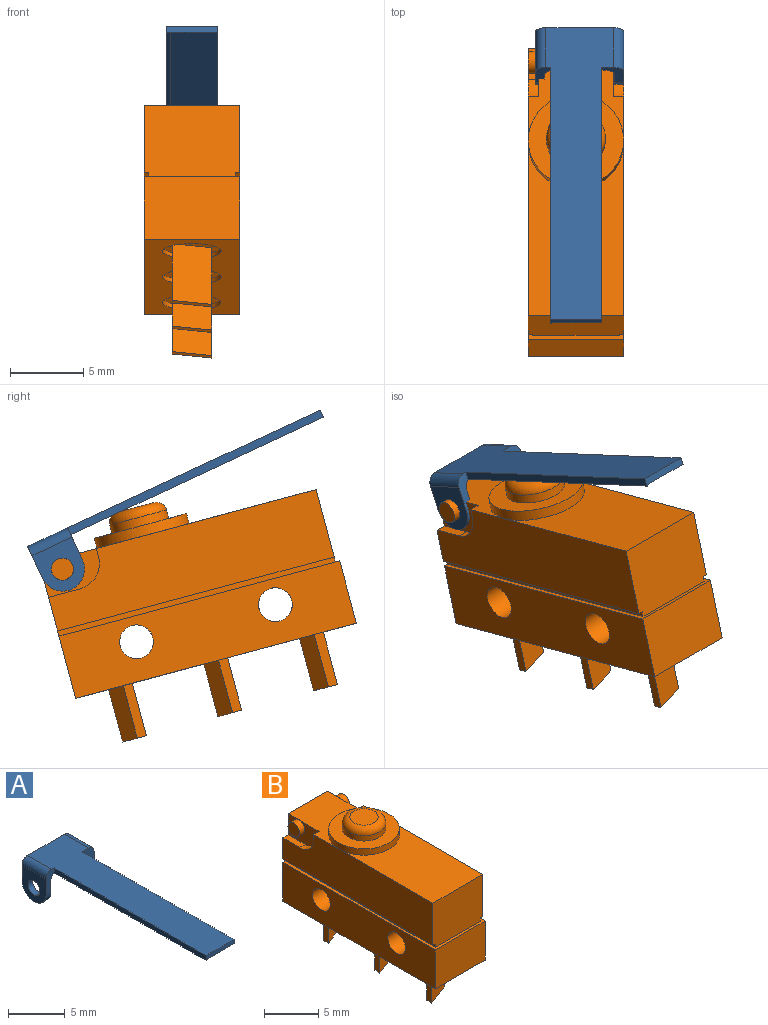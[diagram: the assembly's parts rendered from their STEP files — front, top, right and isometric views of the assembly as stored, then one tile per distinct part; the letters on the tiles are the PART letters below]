
ASSEMBLY  parts=2 mates=1
PART A: 20 faces, bbox 6x22x3.9 mm
  f0: plane 22x3.4mm, normal (0,0,-1), area 71mm2, adj f2,f3,f5,f7,f16,f17
  f1: plane 19x0.53mm, normal (-1,0,0), area 10.1mm2, adj f4,f5,f8,f16
  f2: plane 19x0.46mm, normal (1,0,0), area 8.8mm2, adj f0,f4,f5,f7
  f3: plane 6x2.4mm, normal (0,1,0), area 5.1mm2, adj f0,f4,f6,f9,f10,f12,f13,f15
  f4: plane 22x4.6mm, normal (0,0,1), area 80.3mm2, adj f1,f2,f3,f5,f7,f8,f18,f19
  f5: plane 3.5x0.53mm, normal (0,-1,0), area 1.6mm2, adj f0,f1,f2,f4,f16
  f6: plane 3.2x3mm, normal (1,0,0), area 6.9mm2, adj f3,f7,f10,f11,f18
  f7: plane 2.4x1.5mm, normal (0,-1,0), area 1.9mm2, adj f0,f2,f4,f6,f10,f12,f17,f18
  f8: plane 2.4x1mm, normal (0,-1,0), area 1.6mm2, adj f1,f4,f9,f13,f15,f16,f19
  f9: plane 3.2x3mm, normal (-1,0,0), area 6.9mm2, adj f3,f8,f13,f14,f19
  f10: cylinder r=1.5mm len=3mm, axis (1,0,0), area 2.8mm2, adj f3,f6,f7,f12
  f11: cylinder r=0.75mm len=1.5mm, axis (1,0,0), area 2.8mm2, adj f6,f12
  f12: plane 3x2.74mm, normal (-1,0,0), area 5.5mm2, adj f3,f7,f10,f11,f17
  f13: cylinder r=1.5mm len=3mm, axis (1,0,0), area 2.8mm2, adj f3,f8,f9,f15
  f14: cylinder r=0.75mm len=1.5mm, axis (1,0,0), area 2.8mm2, adj f9,f15
  f15: plane 3x2.74mm, normal (1,0,0), area 5.5mm2, adj f3,f8,f13,f14,f16
  f16: cylinder r=0.7mm len=22mm, axis (0,-1,0), area 9.2mm2, adj f0,f1,f3,f5,f8,f15
  f17: cylinder r=0.7mm len=3mm, axis (0,1,0), area 3.3mm2, adj f0,f3,f7,f12
  f18: cylinder r=0.7mm len=3mm, axis (0,-1,0), area 3.3mm2, adj f3,f4,f6,f7
  f19: cylinder r=0.7mm len=3mm, axis (0,1,0), area 3.3mm2, adj f3,f4,f8,f9
PART B: 55 faces, bbox 6.5x19.8x15.2 mm
  f0: plane 4x4mm, normal (0,0,-1), area 10.8mm2, adj f36,f50,f51,f52,f53
  f1: plane 4x4mm, normal (0,0,-1), area 10.8mm2, adj f37,f45,f46,f47,f48
  f2: plane 12.2x6.5mm, normal (0,0,1), area 62.7mm2, adj f3,f4,f6,f25
  f3: plane 19.5x4.75mm, normal (1,0,0), area 83.8mm2, adj f2,f5,f6,f8,f15,f20,f22,f24
  f4: plane 19.5x4.75mm, normal (-1,0,0), area 83.8mm2, adj f2,f5,f6,f8,f14,f18,f19,f23
  f5: plane 7.3x6.5mm, normal (0,0,1), area 25.3mm2, adj f3,f4,f8,f17,f19,f21,f22,f25
  f6: plane 6.5x5.11mm, normal (0,-1,0), area 33mm2, adj f2,f3,f4,f12,f13,f14,f15,f16
  f7: plane 19.8x4.39mm, normal (1,0,0), area 78.6mm2, adj f8,f10,f11,f12,f30,f31
  f8: plane 9.5x6.5mm, normal (0,1,0), area 58.2mm2, adj f3,f4,f5,f7,f9,f10,f12,f13
  f9: plane 19.8x4.39mm, normal (-1,0,0), area 78.6mm2, adj f8,f10,f11,f12,f30,f31
  f10: plane 19.8x6.5mm, normal (0,0,-1), area 91mm2, adj f7,f8,f9,f11,f36,f37,f38
  f11: plane 6.5x4.39mm, normal (0,-1,0), area 28.5mm2, adj f7,f9,f10,f12
  f12: plane 19.8x6.5mm, normal (0,0,1), area 13.7mm2, adj f6,f7,f8,f9,f11,f13,f16
  f13: plane 19.5x0.36mm, normal (-1,0,0), area 7mm2, adj f6,f8,f12,f14
  f14: plane 19.5x0.3mm, normal (0,0,-1), area 5.8mm2, adj f4,f6,f8,f13
  f15: plane 19.5x0.3mm, normal (0,0,-1), area 5.8mm2, adj f3,f6,f8,f16
  f16: plane 19.5x0.36mm, normal (1,0,0), area 7mm2, adj f6,f8,f12,f15
  f17: plane 4x2.38mm, normal (-1,0,0), area 7mm2, adj f5,f8,f18,f19,f23,f34
  f18: plane 2.2x0.7mm, normal (0,0,1), area 1.5mm2, adj f4,f8,f17,f23
  f19: plane 0.7x0.58mm, normal (0,1,0), area 0.4mm2, adj f4,f5,f17,f23
  f20: plane 2.2x0.7mm, normal (0,0,1), area 1.5mm2, adj f3,f8,f21,f24
  f21: plane 4x2.38mm, normal (1,0,0), area 7mm2, adj f5,f8,f20,f22,f24,f33
  f22: plane 0.7x0.58mm, normal (0,1,0), area 0.4mm2, adj f3,f5,f21,f24
  f23: cylinder r=1.8mm len=1.8mm, axis (-1,0,0), area 2mm2, adj f4,f17,f18,f19
  f24: cylinder r=1.8mm len=1.8mm, axis (-1,0,0), area 2mm2, adj f3,f20,f21,f22
  f25: cylinder r=3.25mm len=6.5mm, axis (0,0,-1), area 14.3mm2, adj f2,f5,f26
  f26: plane 6.5x6.5mm, normal (0,0,1), area 20.6mm2, adj f25,f27
  f27: cylinder r=2mm len=4mm, axis (0,0,-1), area 7.5mm2, adj f26,f29
  f28: plane 2.6x2.6mm, normal (0,0,1), area 5.3mm2, adj f29
  f29: torus R=1.3mm, axis (0,0,1), area 12.1mm2, adj f27,f28
  f30: cylinder r=1.15mm len=6.5mm, axis (1,0,0), area 47mm2, adj f7,f9
  f31: cylinder r=1.15mm len=6.5mm, axis (1,0,0), area 47mm2, adj f7,f9
  f32: plane 1.5x1.5mm, normal (1,0,0), area 1.8mm2, adj f33
  f33: cylinder r=0.75mm len=1.5mm, axis (1,0,0), area 3.3mm2, adj f21,f32
  f34: cylinder r=0.75mm len=1.5mm, axis (1,0,0), area 3.3mm2, adj f17,f35
  f35: plane 1.5x1.5mm, normal (-1,0,0), area 1.8mm2, adj f34
  f36: cylinder r=2mm len=4mm, axis (0,0,-1), area 3.8mm2, adj f0,f10
  f37: cylinder r=2mm len=4mm, axis (0,0,-1), area 3.8mm2, adj f1,f10
  f38: cylinder r=2mm len=4mm, axis (0,0,-1), area 3.8mm2, adj f10,f39
  f39: plane 4x4mm, normal (0,0,-1), area 10.8mm2, adj f38,f40,f41,f42,f43
  f40: plane 4x2.7mm, normal (-0.36,0.93,0), area 11.6mm2, adj f39,f41,f43,f44
  f41: plane 4x0.64mm, normal (1,0,0), area 2.6mm2, adj f39,f40,f42,f44
  f42: plane 4x2.7mm, normal (0.36,-0.93,0), area 11.6mm2, adj f39,f41,f43,f44
  f43: plane 4x0.64mm, normal (-1,0,0), area 2.6mm2, adj f39,f40,f42,f44
  f44: plane 2.7x1.67mm, normal (0,0,-1), area 1.7mm2, adj f40,f41,f42,f43
  f45: plane 4x2.7mm, normal (0.36,-0.93,0), area 11.6mm2, adj f1,f46,f48,f49
  f46: plane 4x0.64mm, normal (-1,0,0), area 2.6mm2, adj f1,f45,f47,f49
  f47: plane 4x2.7mm, normal (-0.36,0.93,0), area 11.6mm2, adj f1,f46,f48,f49
  f48: plane 4x0.64mm, normal (1,0,0), area 2.6mm2, adj f1,f45,f47,f49
  f49: plane 2.7x1.67mm, normal (0,0,-1), area 1.7mm2, adj f45,f46,f47,f48
  f50: plane 4x2.7mm, normal (0.36,-0.93,0), area 11.6mm2, adj f0,f51,f53,f54
  f51: plane 4x0.64mm, normal (-1,0,0), area 2.6mm2, adj f0,f50,f52,f54
  f52: plane 4x2.7mm, normal (-0.36,0.93,0), area 11.6mm2, adj f0,f51,f53,f54
  f53: plane 4x0.64mm, normal (1,0,0), area 2.6mm2, adj f0,f50,f52,f54
  f54: plane 2.7x1.67mm, normal (0,0,-1), area 1.7mm2, adj f50,f51,f52,f53
PLACE A rot(axis=(-1,0,0),25deg) t=(-1.23,-14.71,-3.45)mm
PLACE B rot(axis=(-1,0,0),15deg) t=(-1.23,-8.62,5.36)mm
MATE revolute A.f10 <-> B.f33  axis (1,0,0) through (-1.23,11.41,9.04)mm
